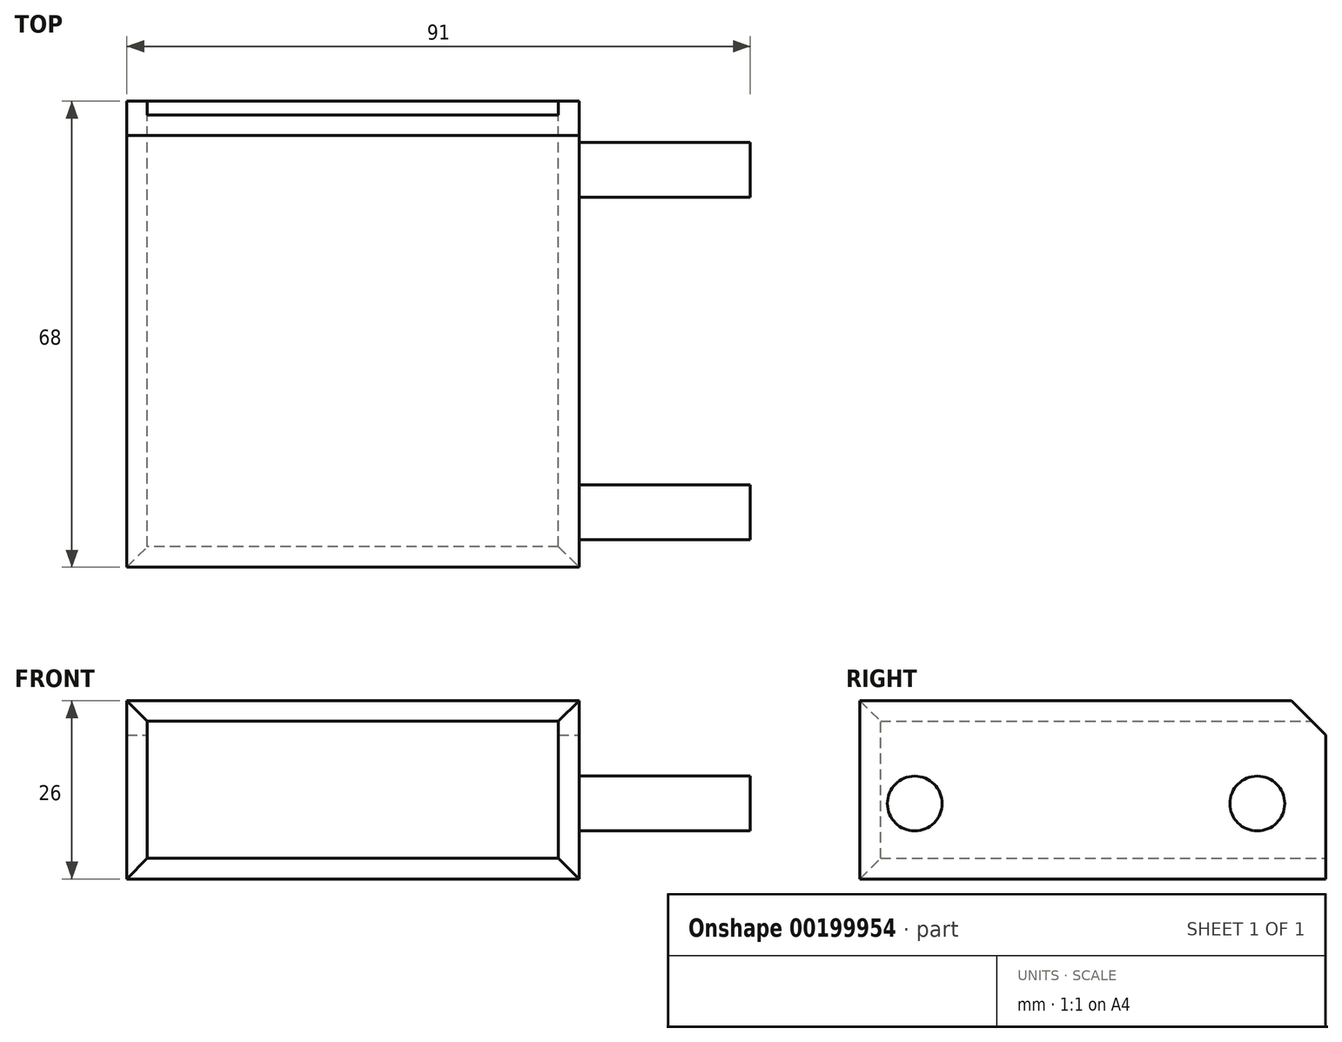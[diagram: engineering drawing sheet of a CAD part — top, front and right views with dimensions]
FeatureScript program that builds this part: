
annotation { "Feature Type Name" : "Feature", "Feature Type Description" : "" }
export const myFeature = defineFeature(function(context is Context, id is Id, definition is map)
    precondition{}
    {
        {
            var Q0;
            Q0=qCreatedBy(makeId("Front.planeOp"),FACE);
            var sketch = newSketch(context, id + "F0", { "sketchPlane" : qUnion([Q0])});
            skLineSegment(sketch, "E0.bottom", {"start": v(34.3, 19.47) * mm, "end": v(-31.7, 19.47) * mm});
            skLineSegment(sketch, "E0.top", {"start": v(34.3, -6.53) * mm, "end": v(-31.7, -6.53) * mm});
            skLineSegment(sketch, "E0.left", {"start": v(34.3, 19.47) * mm, "end": v(34.3, -6.53) * mm});
            skLineSegment(sketch, "E0.right", {"start": v(-31.7, 19.47) * mm, "end": v(-31.7, -6.53) * mm});
            skLineSegment(sketch, "E1.bottom", {"start": v(31.3, 16.47) * mm, "end": v(-28.7, 16.47) * mm});
            skLineSegment(sketch, "E1.top", {"start": v(31.3, -3.53) * mm, "end": v(-28.7, -3.53) * mm});
            skLineSegment(sketch, "E1.left", {"start": v(31.3, 16.47) * mm, "end": v(31.3, -3.53) * mm});
            skLineSegment(sketch, "E1.right", {"start": v(-28.7, 16.47) * mm, "end": v(-28.7, -3.53) * mm});
            skSolve(sketch);
        }
        {
            var Q0;
            Q0 = qSketchRegion(id + "F0", true);
            extrude(context, id + "F1", {"entities" : qUnion([Q0]), "depth" : 70 * mm});
        }
        {
            var Q0;
            Q0=makeQuery(id+"F1.opExtrude","SWEPT_FACE",FACE,{"disambiguationData":[OSD([sQuery(id+"F0.wireOp",EDGE,"E0.left")])]});
            var sketch = newSketch(context, id + "F2", { "sketchPlane" : qUnion([Q0])});
            skCircle(sketch, "E2", {"center": v(-60, 4.47) * mm, "radius": 4 * mm});
            skCircle(sketch, "E3", {"center": v(-10, 4.47) * mm, "radius": 4 * mm});
            skSolve(sketch);
        }
        {
            var Q0;
            Q0 = qSketchRegion(id + "F2", true);
            extrude(context, id + "F3", {"entities" : qUnion([Q0]), "operationType" : NewBodyOperationType.ADD, "depth" : 25 * mm});
        }
        {
            var Q0;
            Q0=makeQuery(id+"F1.opExtrude","CAP_EDGE",EDGE,{"disambiguationData":[OSD([sQuery(id+"F0.wireOp",EDGE,"E1.bottom")])],"isStart":false});
            var Q1;
            Q1=makeQuery(id+"F1.opExtrude","CAP_EDGE",EDGE,{"disambiguationData":[OSD([sQuery(id+"F0.wireOp",EDGE,"E1.right")])],"isStart":false});
            var Q2;
            Q2=makeQuery(id+"F1.opExtrude","CAP_EDGE",EDGE,{"disambiguationData":[OSD([sQuery(id+"F0.wireOp",EDGE,"E1.top")])],"isStart":false});
            var Q3;
            Q3=makeQuery(id+"F1.opExtrude","CAP_EDGE",EDGE,{"disambiguationData":[OSD([sQuery(id+"F0.wireOp",EDGE,"E1.left")])],"isStart":false});
            chamfer(context, id + "F4", {"entities" : qUnion([Q0, Q1, Q2, Q3]), "width" : 5 * mm, "tangentPropagation" : true});
        }
        {
            var Q0;
            Q0=makeQuery(id+"F1.opExtrude","CAP_EDGE",EDGE,{"disambiguationData":[OSD([sQuery(id+"F0.wireOp",EDGE,"E0.bottom")])],"isStart":true});
            chamfer(context, id + "F5", {"entities" : qUnion([Q0]), "width" : 5 * mm, "tangentPropagation" : true});
        }
    });
